# Revit family: 380000
name_source: partatom
category: Specialty Equipment
revit_build: Autodesk Revit 2018 (Build: 20170223_1515(x64)
units: mm (PartAtom-declared; Revit-internal decimal feet)

## family parameters
Cut with Voids When Loaded = No
Host = Face
OmniClass Number = 23.40.20.21.14
OmniClass Title = Hand and Hair Dryers
Part Type = Normal
Room Calculation Point = No
Round Connector Dimension = Use Diameter
Shared = No

## types (3) — shared parameters
Default Elevation = 1' - 5 9/16"
Depth = 0' - 0 1/16"
Description = Wall Guard
Height = 2' - 8"
Keynote = 10 28 13
Manufacturer = Excel Dryer
Manufacturer Fax Number = 1-413-525-2853
Product Documentation Link = http://www.exceldryer.com
Product Name = XLERATOR Wall Guard
Product Page URL = http://www.exceldryer.com
URL = http://www.exceldryer.com
Version = 2017 - v1.0b
Width = 1' - 4"

## per-type parameters (varying)
| type | Assembly Code | Material | Model | Wall Guard Material |
| 89S | C1030200 | Stainless Steel | Wall Guard Stainless | Metal - Excel Dryer - Stainless Steel - Brushed |
| 89B | C1030200 | Microban anti-microbial plastic | Wall Guard Black | Plastic - Excel Dryer - Anti-Microbial - Black |
| 89W | C1090.4040 | Microban anti-microbial plastic | Wall Guard White | Plastic - Excel Dryer - Anti-Microbial - White |

## geometry (parser evidence)
native form markers: Sweep x2
no freeform markers — native parametric forms only
